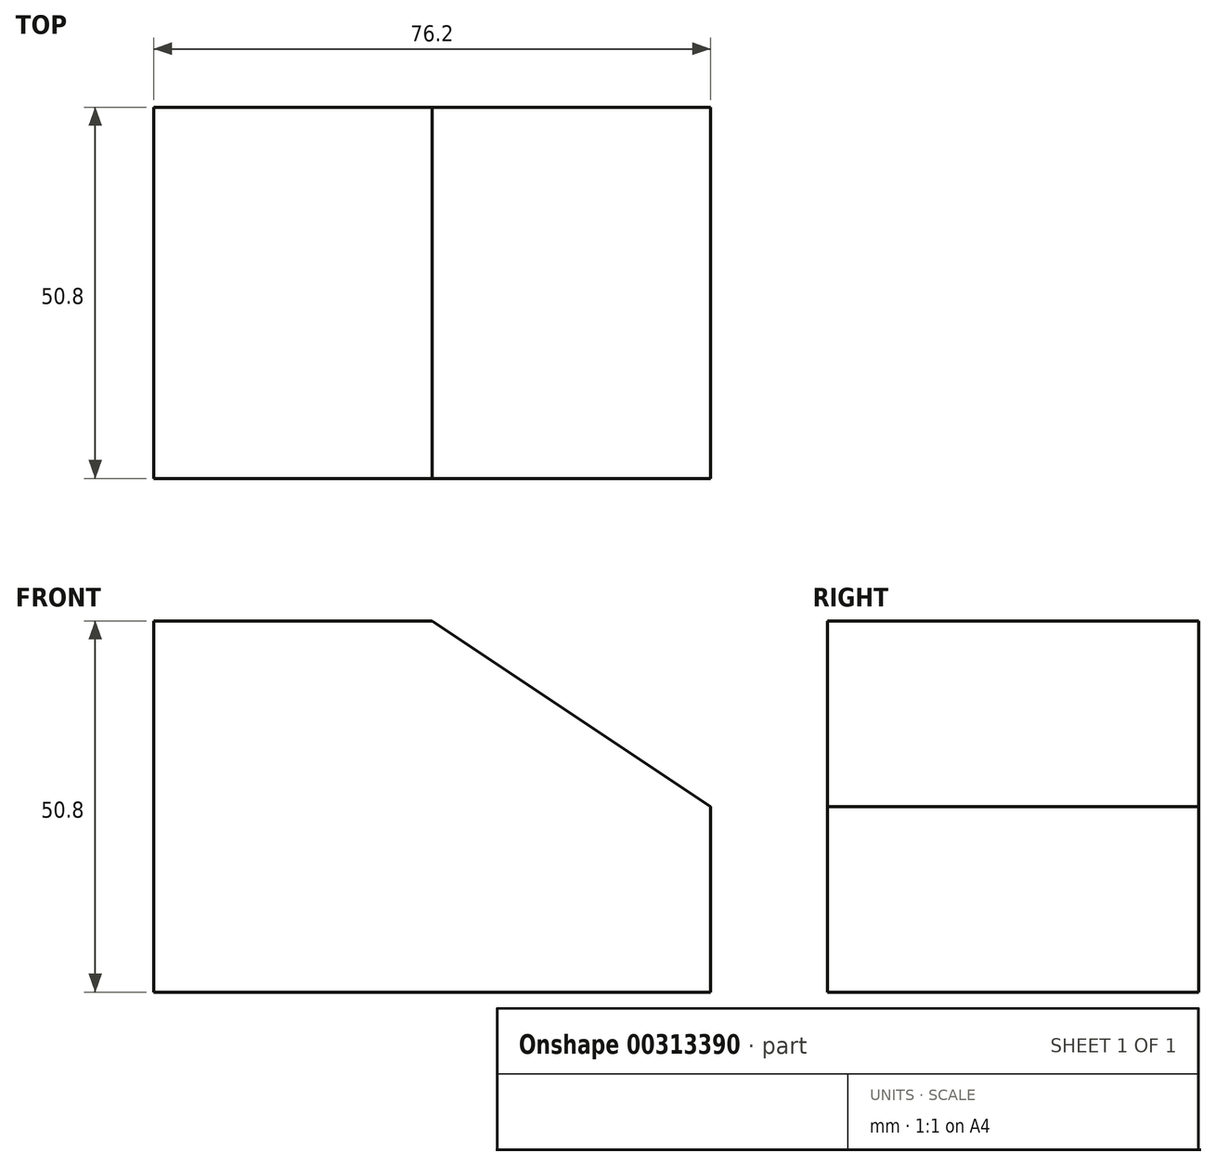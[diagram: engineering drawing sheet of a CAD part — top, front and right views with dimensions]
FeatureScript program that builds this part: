
annotation { "Feature Type Name" : "Feature", "Feature Type Description" : "" }
export const myFeature = defineFeature(function(context is Context, id is Id, definition is map)
    precondition{}
    {
        {
            var Q0;
            Q0=qCreatedBy(makeId("Front.planeOp"),FACE);
            var sketch = newSketch(context, id + "F0", { "sketchPlane" : qUnion([Q0])});
            skLineSegment(sketch, "E0", {"start": v(-40.27, -61.13) * mm, "end": v(35.93, -61.13) * mm});
            skLineSegment(sketch, "E1", {"start": v(35.93, -61.13) * mm, "end": v(35.93, -35.73) * mm});
            skLineSegment(sketch, "E2", {"start": v(-40.27, -61.13) * mm, "end": v(-40.27, -10.33) * mm});
            skLineSegment(sketch, "E3", {"start": v(-40.27, -10.33) * mm, "end": v(-2.17, -10.33) * mm});
            skLineSegment(sketch, "E4", {"start": v(-2.17, -10.33) * mm, "end": v(35.93, -35.73) * mm});
            skSolve(sketch);
        }
        {
            var Q0;
            Q0=makeQuery(id+"F0.imprint","IMPRINT",FACE,{"disambiguationData":[TD([[makeQuery(id+"F0.imprint","IMPRINT",EDGE,{"derivedFrom":sQuery(id+"F0.wireOp",EDGE,"E0")}),1.0]])]});
            extrude(context, id + "F1", {"entities" : qUnion([Q0]), "depth" : 50.8 * mm});
        }
    });
